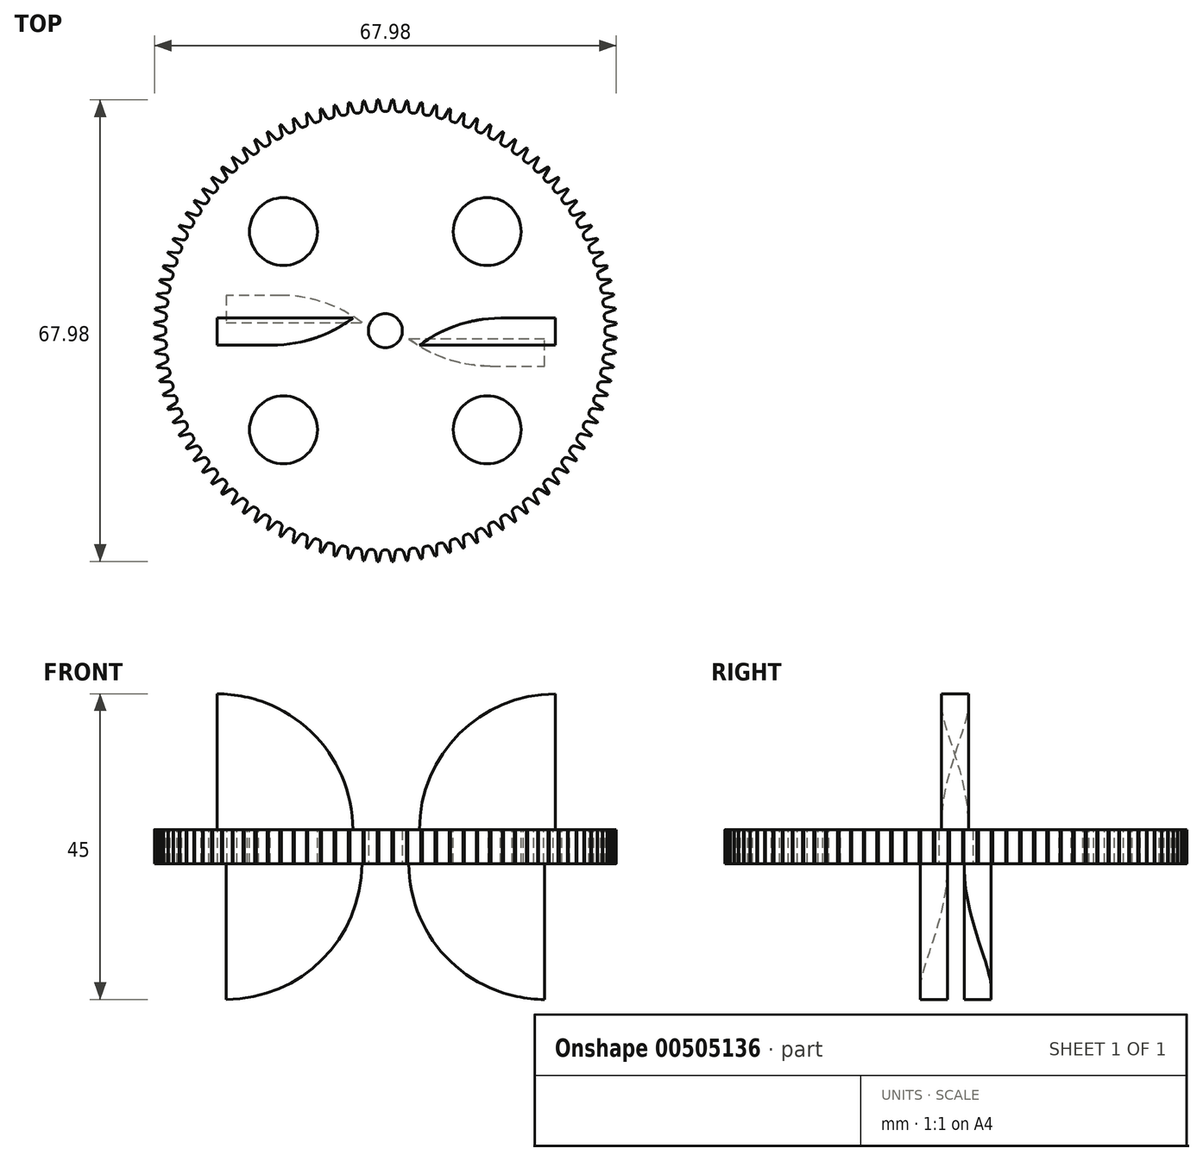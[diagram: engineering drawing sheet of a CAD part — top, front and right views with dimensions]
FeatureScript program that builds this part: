
annotation { "Feature Type Name" : "Feature", "Feature Type Description" : "" }
export const myFeature = defineFeature(function(context is Context, id is Id, definition is map)
    precondition{}
    {
        {
            var Q0;
            Q0=qCreatedBy(makeId("Top.planeOp"),FACE);
            var sketch = newSketch(context, id + "F0", { "sketchPlane" : qUnion([Q0])});
            skCircle(sketch, "E0", {"center": v(0, 0) * mm, "radius": 34 * mm});
            skCircle(sketch, "E1", {"center": v(0, 0) * mm, "radius": 2.5 * mm});
            skSolve(sketch);
        }
        {
            var Q0;
            Q0=makeQuery(id+"F0.imprint","IMPRINT",FACE,{"disambiguationData":[TD([[makeQuery(id+"F0.imprint","IMPRINT",EDGE,{"derivedFrom":sQuery(id+"F0.wireOp",EDGE,"E0")}),1.0]])]});
            extrude(context, id + "F1", {"entities" : qUnion([Q0]), "depth" : 5 * mm, "offsetDistance" : 25 * mm});
        }
        {
            var Q0;
            Q0=makeQuery(id+"F1.opExtrude","CAP_FACE",FACE,{"disambiguationData":[OSD([sQuery(id+"F0.wireOp",EDGE,"E0"),sQuery(id+"F0.wireOp",EDGE,"E1")])],"isStart":false});
            var sketch = newSketch(context, id + "F2", { "sketchPlane" : qUnion([Q0])});
            skLineSegment(sketch, "E2", {"start": v(0, 0) * mm, "end": v(0, 34) * mm, "construction": true});
            skLineSegment(sketch, "E3", {"start": v(-0.95, 33.99) * mm, "end": v(-0.6, 32.67) * mm});
            skLineSegment(sketch, "E4.MirrorCS", {"start": v(0.95, 33.99) * mm, "end": v(0.6, 32.67) * mm});
            skLineSegment(sketch, "E5", {"start": v(-0.12, 32.3) * mm, "end": v(0.12, 32.3) * mm});
            skPoint(sketch, "E6.visualSharp", {"position": v(-0.5, 32.3) * mm});
            skArc(sketch, "E6.filletArc", {"start": v(-0.6, 32.67) * mm, "mid": v(-0.42, 32.4) * mm, "end": v(-0.12, 32.3) * mm});
            skPoint(sketch, "E7.visualSharp", {"position": v(0.5, 32.3) * mm});
            skArc(sketch, "E7.filletArc", {"start": v(0.12, 32.3) * mm, "mid": v(0.42, 32.4) * mm, "end": v(0.6, 32.67) * mm});
            skSolve(sketch);
        }
        {
            var Q0;
            {var subQ1=sQuery(id+"F2.wireOp",EDGE,"E3");Q0=makeQuery(id+"F2.imprint","IMPRINT",FACE,{"disambiguationData":[TD([[makeQuery(id+"F2.imprint","IMPRINT",EDGE,{"derivedFrom":subQ1}),1.0]])]});}
            extrude(context, id + "F3", {"entities" : qUnion([Q0]), "operationType" : NewBodyOperationType.REMOVE, "oppositeDirection" : true, "depth" : 25 * mm, "offsetDistance" : 25 * mm});
        }
        {
            var Q0;
            Q0=makeQuery(id+"F3.boolean.opBoolean","COPY",FACE,{"derivedFrom":makeQuery(id+"F3.opExtrude","SWEPT_FACE",FACE,{"disambiguationData":[OSD([sQuery(id+"F2.wireOp",EDGE,"E4.MirrorCS")])]})});
            var Q1;
            Q1=makeQuery(id+"F3.boolean.opBoolean","COPY",FACE,{"derivedFrom":makeQuery(id+"F3.opExtrude","SWEPT_FACE",FACE,{"disambiguationData":[OSD([sQuery(id+"F2.wireOp",EDGE,"E7.filletArc")])]})});
            var Q2;
            Q2=makeQuery(id+"F3.boolean.opBoolean","COPY",FACE,{"derivedFrom":makeQuery(id+"F3.opExtrude","SWEPT_FACE",FACE,{"disambiguationData":[OSD([sQuery(id+"F2.wireOp",EDGE,"E5")])]})});
            var Q3;
            Q3=makeQuery(id+"F3.boolean.opBoolean","COPY",FACE,{"derivedFrom":makeQuery(id+"F3.opExtrude","SWEPT_FACE",FACE,{"disambiguationData":[OSD([sQuery(id+"F2.wireOp",EDGE,"E6.filletArc")])]})});
            var Q4;
            Q4=makeQuery(id+"F3.boolean.opBoolean","COPY",FACE,{"derivedFrom":makeQuery(id+"F3.opExtrude","SWEPT_FACE",FACE,{"disambiguationData":[OSD([sQuery(id+"F2.wireOp",EDGE,"E3")])]})});
            var Q5;
            Q5=makeQuery(id+"F1.opExtrude","SWEPT_FACE",FACE,{"disambiguationData":[OSD([sQuery(id+"F0.wireOp",EDGE,"E0")])]});
            circularPattern(context, id + "F4", {"patternType" : PatternType.FACE, "faces" : qUnion([Q0, Q1, Q2, Q3, Q4]), "axis" : qUnion([Q5]), "angle" : 360 * degree, "instanceCount" : 200, "equalSpace" : true});
        }
        {
            var Q0;
            Q0=makeQuery(id+"F1.opExtrude","CAP_FACE",FACE,{"disambiguationData":[OSD([sQuery(id+"F0.wireOp",EDGE,"E0"),sQuery(id+"F0.wireOp",EDGE,"E1")])],"isStart":false});
            var sketch = newSketch(context, id + "F5", { "sketchPlane" : qUnion([Q0])});
            skLineSegment(sketch, "E8", {"start": v(0.12, 32.3) * mm, "end": v(0.12, -32.3) * mm});
            skLineSegment(sketch, "E9", {"start": v(-32.3, 0.12) * mm, "end": v(32.3, 0.12) * mm});
            skLineSegment(sketch, "E10", {"start": v(-24.79, 1.86) * mm, "end": v(-24.79, -2.14) * mm});
            skLineSegment(sketch, "E11", {"start": v(-24.79, -2.14) * mm, "end": v(-4.79, -2.14) * mm});
            skLineSegment(sketch, "E12", {"start": v(-4.79, -2.14) * mm, "end": v(-4.79, 1.86) * mm});
            skLineSegment(sketch, "E13", {"start": v(-4.79, 1.86) * mm, "end": v(-24.79, 1.86) * mm});
            skLineSegment(sketch, "E14.MirrorCS", {"start": v(5.02, -2.14) * mm, "end": v(5.02, 1.86) * mm});
            skLineSegment(sketch, "E15.MirrorCS", {"start": v(25.02, 1.86) * mm, "end": v(25.02, -2.14) * mm});
            skLineSegment(sketch, "E16.MirrorCS", {"start": v(5.02, 1.86) * mm, "end": v(25.02, 1.86) * mm});
            skLineSegment(sketch, "E17.MirrorCS", {"start": v(25.02, -2.14) * mm, "end": v(5.02, -2.14) * mm});
            skLineSegment(sketch, "E18.MirrorCS", {"start": v(32.53, 0.12) * mm, "end": v(-32.06, 0.12) * mm});
            skSolve(sketch);
        }
        {
            var Q0;
            Q0 = qSketchRegion(id + "F5", true);
            extrude(context, id + "F6", {"entities" : qUnion([Q0]), "operationType" : NewBodyOperationType.ADD, "depth" : 20 * mm, "offsetDistance" : 25 * mm});
        }
        {
            var Q0;
            Q0=makeQuery(id+"F6.opExtrude","CAP_EDGE",EDGE,{"disambiguationData":[OSD([sQuery(id+"F5.wireOp",EDGE,"E12")])],"isStart":false});
            var Q1;
            Q1=makeQuery(id+"F6.opExtrude","SWEPT_EDGE",EDGE,{"disambiguationData":[OSD([sQuery(id+"F5.wireOp",EDGE,"E11"),sQuery(id+"F5.wireOp",EDGE,"E12")])]});
            fillet(context, id + "F7", {"entities" : qUnion([Q0, Q1]), "radius" : 20 * mm, "tangentPropagation" : true, "allowEdgeOverflow" : false});
        }
        {
            var Q0;
            Q0=makeQuery(id+"F6.opExtrude","SWEPT_EDGE",EDGE,{"disambiguationData":[OSD([sQuery(id+"F5.wireOp",EDGE,"E14.MirrorCS"),sQuery(id+"F5.wireOp",EDGE,"E16.MirrorCS")])]});
            var Q1;
            Q1=makeQuery(id+"F6.opExtrude","CAP_EDGE",EDGE,{"disambiguationData":[OSD([sQuery(id+"F5.wireOp",EDGE,"E14.MirrorCS")])],"isStart":false});
            fillet(context, id + "F8", {"entities" : qUnion([Q0, Q1]), "radius" : 20 * mm, "tangentPropagation" : true, "allowEdgeOverflow" : false});
        }
        {
            var Q0;
            Q0=makeQuery(id+"F1.opExtrude","CAP_FACE",FACE,{"disambiguationData":[OSD([sQuery(id+"F0.wireOp",EDGE,"E0"),sQuery(id+"F0.wireOp",EDGE,"E1")])],"isStart":true});
            var sketch = newSketch(context, id + "F9", { "sketchPlane" : qUnion([Q0])});
            skLineSegment(sketch, "E19", {"start": v(0, -13.64) * mm, "end": v(0, 18.2) * mm, "construction": true});
            skLineSegment(sketch, "E20", {"start": v(-19.75, 0) * mm, "end": v(20.94, 0) * mm, "construction": true});
            skLineSegment(sketch, "E21", {"start": v(3.46, 1.2) * mm, "end": v(3.46, 5.2) * mm});
            skLineSegment(sketch, "E22", {"start": v(3.46, 5.2) * mm, "end": v(23.46, 5.2) * mm});
            skLineSegment(sketch, "E23", {"start": v(23.46, 5.2) * mm, "end": v(23.46, 1.2) * mm});
            skLineSegment(sketch, "E24", {"start": v(23.46, 1.2) * mm, "end": v(3.46, 1.2) * mm});
            skLineSegment(sketch, "E25.MirrorCS", {"start": v(-3.46, -1.2) * mm, "end": v(-3.46, -5.2) * mm});
            skLineSegment(sketch, "E26.MirrorCS", {"start": v(-23.46, -1.2) * mm, "end": v(-3.46, -1.2) * mm});
            skLineSegment(sketch, "E27.MirrorCS", {"start": v(-3.46, -5.2) * mm, "end": v(-23.46, -5.2) * mm});
            skLineSegment(sketch, "E28.MirrorCS", {"start": v(-23.46, -5.2) * mm, "end": v(-23.46, -1.2) * mm});
            skSolve(sketch);
        }
        {
            var Q0;
            Q0 = qSketchRegion(id + "F9", true);
            extrude(context, id + "F10", {"entities" : qUnion([Q0]), "operationType" : NewBodyOperationType.ADD, "depth" : 20 * mm, "offsetDistance" : 25 * mm});
        }
        {
            var Q0;
            Q0 = qSketchRegion(id + "F9", true);
            extrude(context, id + "F11", {"entities" : qUnion([Q0]), "operationType" : NewBodyOperationType.ADD, "depth" : 20 * mm, "offsetDistance" : 25 * mm});
        }
        {
            var Q0;
            Q0=makeQuery(id+"F10.opExtrude","CAP_EDGE",EDGE,{"disambiguationData":[OSD([sQuery(id+"F9.wireOp",EDGE,"E21")])],"isStart":false});
            var Q1;
            Q1=makeQuery(id+"F10.opExtrude","SWEPT_EDGE",EDGE,{"disambiguationData":[OSD([sQuery(id+"F9.wireOp",EDGE,"E21"),sQuery(id+"F9.wireOp",EDGE,"E22")])]});
            var Q2;
            Q2=makeQuery(id+"F10.opExtrude","SWEPT_EDGE",EDGE,{"disambiguationData":[OSD([sQuery(id+"F9.wireOp",EDGE,"E25.MirrorCS"),sQuery(id+"F9.wireOp",EDGE,"E27.MirrorCS")])]});
            var Q3;
            Q3=makeQuery(id+"F10.opExtrude","CAP_EDGE",EDGE,{"disambiguationData":[OSD([sQuery(id+"F9.wireOp",EDGE,"E25.MirrorCS")])],"isStart":false});
            fillet(context, id + "F12", {"entities" : qUnion([Q0, Q1, Q2, Q3]), "radius" : 20 * mm, "tangentPropagation" : true, "allowEdgeOverflow" : false});
        }
        {
            var Q0;
            Q0=makeQuery(id+"F1.opExtrude","CAP_FACE",FACE,{"disambiguationData":[OSD([sQuery(id+"F0.wireOp",EDGE,"E0"),sQuery(id+"F0.wireOp",EDGE,"E1")])],"isStart":false});
            var sketch = newSketch(context, id + "F13", { "sketchPlane" : qUnion([Q0])});
            skCircle(sketch, "E29", {"center": v(-15, 14.6) * mm, "radius": 5 * mm});
            skCircle(sketch, "E30.MirrorC", {"center": v(15, 14.6) * mm, "radius": 5 * mm});
            skCircle(sketch, "E31.MirrorC", {"center": v(-15, -14.6) * mm, "radius": 5 * mm});
            skCircle(sketch, "E32.MirrorC", {"center": v(15, -14.6) * mm, "radius": 5 * mm});
            skSolve(sketch);
        }
        {
            var Q0;
            Q0 = qSketchRegion(id + "F13", true);
            extrude(context, id + "F14", {"entities" : qUnion([Q0]), "operationType" : NewBodyOperationType.REMOVE, "oppositeDirection" : true, "depth" : 25 * mm, "offsetDistance" : 25 * mm});
        }
    });
